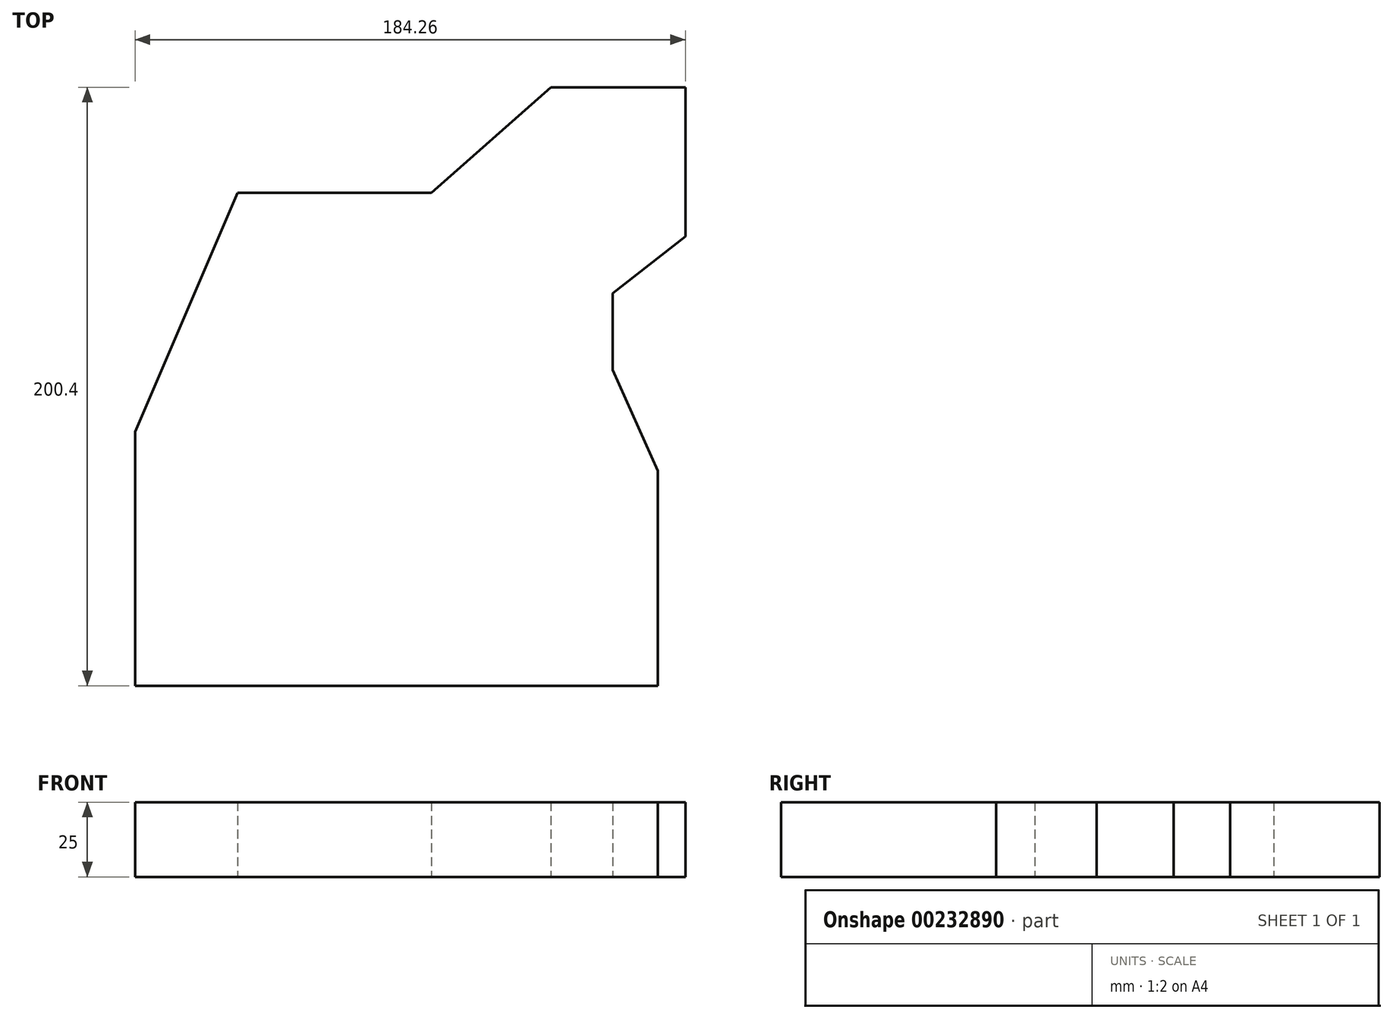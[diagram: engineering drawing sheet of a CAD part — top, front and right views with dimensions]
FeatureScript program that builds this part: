
annotation { "Feature Type Name" : "Feature", "Feature Type Description" : "" }
export const myFeature = defineFeature(function(context is Context, id is Id, definition is map)
    precondition{}
    {
        {
            var Q0;
            Q0=qCreatedBy(makeId("Top.planeOp"),FACE);
            var sketch = newSketch(context, id + "F0", { "sketchPlane" : qUnion([Q0])});
            skLineSegment(sketch, "E0", {"start": v(-92.2, -92.93) * mm, "end": v(82.8, -92.93) * mm});
            skLineSegment(sketch, "E1", {"start": v(-92.2, -92.93) * mm, "end": v(-92.2, -7.93) * mm});
            skLineSegment(sketch, "E2", {"start": v(-92.2, -7.93) * mm, "end": v(-57.94, 72.07) * mm});
            skLineSegment(sketch, "E3", {"start": v(-57.94, 72.07) * mm, "end": v(7.06, 72.07) * mm});
            skLineSegment(sketch, "E4", {"start": v(7.06, 72.07) * mm, "end": v(47.06, 107.47) * mm});
            skLineSegment(sketch, "E5", {"start": v(47.06, 107.47) * mm, "end": v(92.06, 107.47) * mm});
            skLineSegment(sketch, "E6", {"start": v(92.06, 107.47) * mm, "end": v(92.06, 57.47) * mm});
            skLineSegment(sketch, "E7", {"start": v(92.06, 57.47) * mm, "end": v(67.74, 38.53) * mm});
            skLineSegment(sketch, "E8", {"start": v(67.74, 38.53) * mm, "end": v(67.74, 12.8) * mm});
            skLineSegment(sketch, "E9", {"start": v(82.8, -92.93) * mm, "end": v(82.8, -20.92) * mm});
            skLineSegment(sketch, "E10", {"start": v(67.74, 12.8) * mm, "end": v(82.8, -20.92) * mm});
            skSolve(sketch);
        }
        {
            var Q0;
            Q0=makeQuery(id+"F0.imprint","IMPRINT",FACE,{"disambiguationData":[TD([[makeQuery(id+"F0.imprint","IMPRINT",EDGE,{"derivedFrom":sQuery(id+"F0.wireOp",EDGE,"E0")}),1.0]])]});
            extrude(context, id + "F1", {"entities" : qUnion([Q0]), "depth" : 25 * mm});
        }
    });
